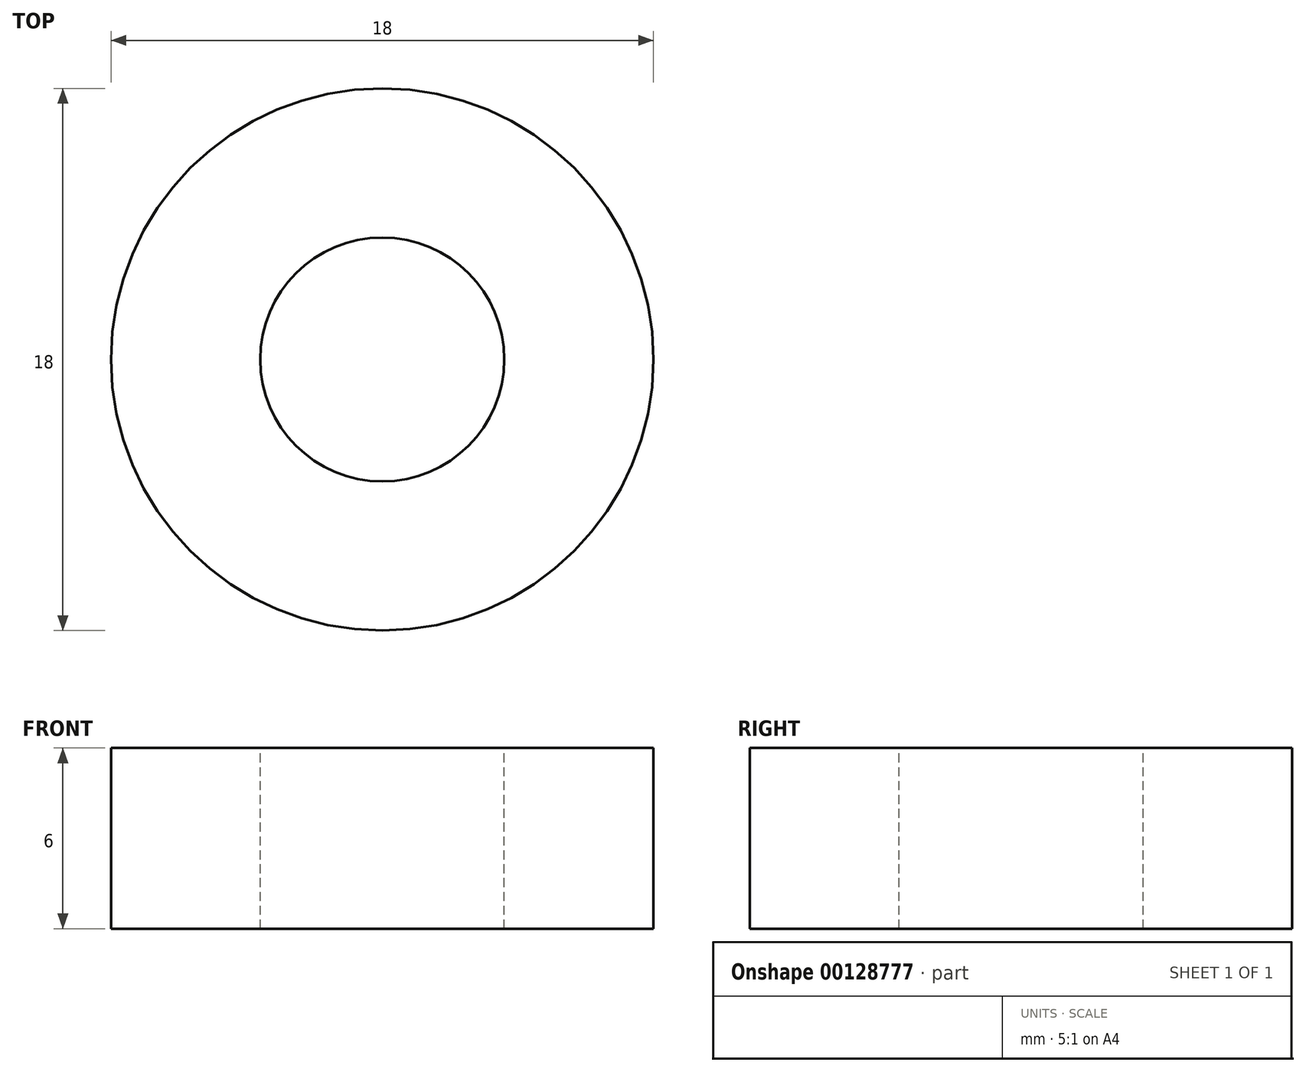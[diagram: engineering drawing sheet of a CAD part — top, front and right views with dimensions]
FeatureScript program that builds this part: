
annotation { "Feature Type Name" : "Feature", "Feature Type Description" : "" }
export const myFeature = defineFeature(function(context is Context, id is Id, definition is map)
    precondition{}
    {
        {
            var Q0;
            Q0=qCreatedBy(makeId("Front.planeOp"),FACE);
            var sketch = newSketch(context, id + "F0", { "sketchPlane" : qUnion([Q0])});
            skLineSegment(sketch, "E0.bottom", {"start": v(-4.05, 0) * mm, "end": v(-9, 0) * mm});
            skLineSegment(sketch, "E0.top", {"start": v(-4.05, 6) * mm, "end": v(-9, 6) * mm});
            skLineSegment(sketch, "E0.left", {"start": v(-4.05, 0) * mm, "end": v(-4.05, 6) * mm});
            skLineSegment(sketch, "E0.right", {"start": v(-9, 0) * mm, "end": v(-9, 6) * mm});
            skLineSegment(sketch, "E1", {"start": v(0, 20.58) * mm, "end": v(0, 0) * mm, "construction": true});
            skSolve(sketch);
        }
        {
            var Q0;
            Q0=makeQuery(id+"F0.imprint","IMPRINT",FACE,{"disambiguationData":[TD([[makeQuery(id+"F0.imprint","IMPRINT",EDGE,{"derivedFrom":sQuery(id+"F0.wireOp",EDGE,"E0.bottom")}),-1.0]])]});
            var Q1;
            Q1=sQuery(id+"F0.wireOp",EDGE,"E1");
            revolve(context, id + "F1", {"entities" : qUnion([Q0]), "axis" : qUnion([Q1]), "revolveType" : RevolveType.FULL});
        }
    });
